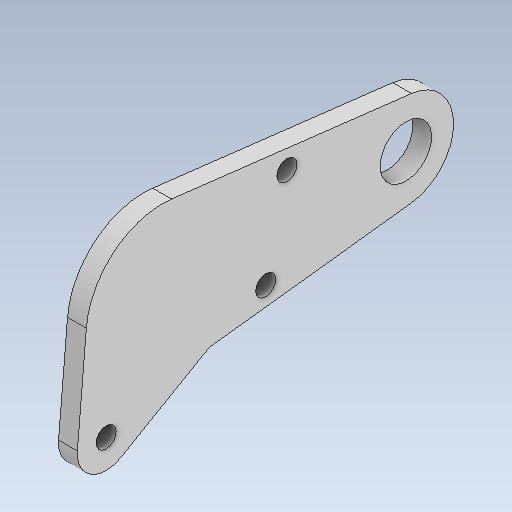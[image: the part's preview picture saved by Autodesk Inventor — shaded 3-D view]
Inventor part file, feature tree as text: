
AUTODESK INVENTOR PART (.ipt)
format: ipt  version: 2020 (Build 240168000, 168)  size: 233,472 bytes
history: native  units: mm
features: extrude x5, sketch x4, projected_geometry x3
ambient origin geometry x8: Origin, YZ Plane, XZ Plane, XY Plane, X Axis, Y Axis, Z Axis, Center Point
bodies: Body1 (feature_tree)
feature tree (12):
  extrude  "Выдавливание4"  Depth=18.6mm
  extrude  "Выдавливание5"  Depth=12.2mm
  extrude  "Выдавливание6"  Depth=9.7mm
  extrude  "Выдавливание7"  Depth=7.1mm
  extrude  "Выдавливание8"  Depth=38.82013mm
  sketch  "Эскиз4"
  projected_geometry  "Спроецированная петля3"
  sketch  "Эскиз5"
  sketch  "Эскиз6"
  projected_geometry  "Спроецированная петля4"
  sketch  "Эскиз7"
  projected_geometry  "Спроецированная петля5"
